# Revit family: R 5 G
name_source: partatom
category: Equipement spécialisé
revit_build: Autodesk Revit LT 2017 (Build: 20160225_1515(x64)
units: mm (PartAtom-declared; Revit-internal decimal feet)

## family parameters
Basée sur le plan de construction = Non
Cote de connecteur circulaire = Utiliser le rayon
Couper avec des vides une fois chargée = Non
Numéro OmniClass = 23.40.40.14.14.11
Partagée = Non
Point de calcul de pièce = Non
Titre OmniClass = Food Mixers
Toujours verticalement = Oui
Type d'élément = Normal

## types (6) — shared parameters
Apparent Power = 0 VA
Depth = 348 mm  [stored 1.14173 ft]
Fabricant = ROBOT COUPE
Height = 508 mm
Modèle = R 5 G
URL = www.robot-coupe.com
Weight = 30 kg
Width = 278 mm
Width Electrique connexion = 173 mm
water = Connector
zero-valued in all types: Cold water supply, Cold water supply height, Used water, Waste water height

## per-type parameters (varying)
| type | Amps | Cycle | Description | HP | Phase | Speeds (Rpm) | Volts | Watts |
| R 5 G    400/50/3 | 2.7 A - 3.4 A | 50 Hz | CUTTER |  | 3 | 1500 and 3000 | 400 V | 1500 W |
| R 5 G    220/60/3 | 4.7 A - 8.8 A | 60 Hz | CUTTERS | 1.5 a 3HP | 3 | 750 and 1500 | 220 V | 2200 W |
| R 5 G    380/60/3 | 2.5 A - 3.5 A | 60 Hz | CUTTER |  | 3 | 1800 and 3600 | 380 V | 1500 W |
| R 5 G    230-400/50/3 | 2.7 A - 3.5 A | 50 Hz | CUTTER |  | 3 | 1500 and 3000 | 400 V | 1500 W |
| R 5 G    220/60/1 | 5.5 A | 60 Hz | CUTTER |  | 1 | 3600 | 220 V | 750 W |
| R 5 G    230/50/1 | 5.1 A | 50 Hz | CUTTER |  | 1 | 3000 | 230 V | 750 W |

note: [stored X ft] marks values corroborated as IEEE doubles in the binary element streams (Revit-internal decimal feet)

## geometry (parser evidence)
native form markers: Sweep x5
no freeform markers — native parametric forms only
